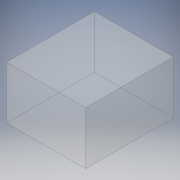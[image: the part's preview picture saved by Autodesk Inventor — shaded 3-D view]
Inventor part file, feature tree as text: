
AUTODESK INVENTOR PART (.ipt)
format: ipt  version: 2017 (Build 210142000, 142)  size: 93,696 bytes
history: native  units: in
note: dims shown in document units (in); Inventor stores cm internally (conversion verified against a paired STEP export)
features: extrude x1, sketch x1
ambient origin geometry x8: Origin, YZ Plane, XZ Plane, XY Plane, X Axis, Y Axis, Z Axis, Center Point
bodies: Solid1 (feature_tree)
feature tree (2):
  extrude  "Extrusion1"  Depth=36.0in
  sketch  "Sketch1"  dims[d0=40.0in d1=36.0in d2=24.0in d3=0.0in]
